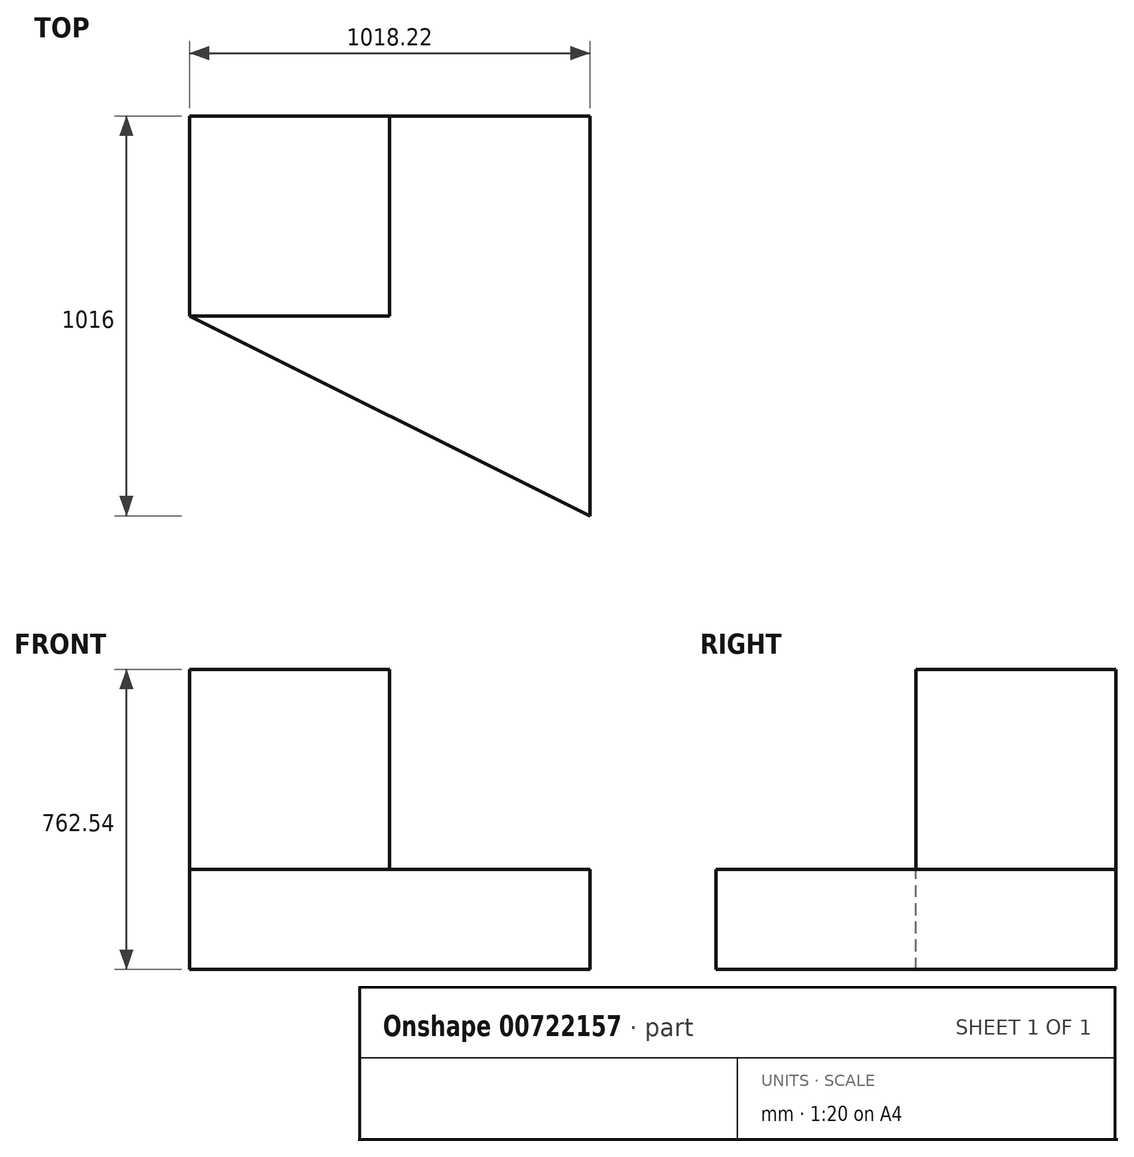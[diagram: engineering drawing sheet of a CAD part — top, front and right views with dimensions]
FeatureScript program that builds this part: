
annotation { "Feature Type Name" : "Feature", "Feature Type Description" : "" }
export const myFeature = defineFeature(function(context is Context, id is Id, definition is map)
    precondition{}
    {
        {
            var Q0;
            Q0=qCreatedBy(makeId("Front.planeOp"),FACE);
            var sketch = newSketch(context, id + "F0", { "sketchPlane" : qUnion([Q0])});
            skLineSegment(sketch, "E0", {"start": v(0, 0) * mm, "end": v(0, 762.54) * mm});
            skLineSegment(sketch, "E1", {"start": v(0, 762.54) * mm, "end": v(1018.22, 762.54) * mm});
            skLineSegment(sketch, "E2", {"start": v(1018.22, 762.54) * mm, "end": v(1018.22, 0) * mm});
            skLineSegment(sketch, "E3", {"start": v(1018.22, 0) * mm, "end": v(0, 0) * mm});
            skSolve(sketch);
        }
        {
            var Q0;
            Q0=makeQuery(id+"F0.imprint","IMPRINT",FACE,{"disambiguationData":[TD([[makeQuery(id+"F0.imprint","IMPRINT",EDGE,{"derivedFrom":sQuery(id+"F0.wireOp",EDGE,"E0")}),-1.0]])]});
            extrude(context, id + "F1", {"entities" : qUnion([Q0]), "depth" : 1016 * mm, "offsetDistance" : 25.4 * mm});
        }
        {
            var Q0;
            Q0=makeQuery(id+"F1.opExtrude","SWEPT_FACE",FACE,{"disambiguationData":[OSD([sQuery(id+"F0.wireOp",EDGE,"E1")])]});
            var sketch = newSketch(context, id + "F2", { "sketchPlane" : qUnion([Q0])});
            skLineSegment(sketch, "E4", {"start": v(0, -508) * mm, "end": v(0, -1016) * mm});
            skLineSegment(sketch, "E5", {"start": v(0, -1016) * mm, "end": v(1018.22, -1016) * mm});
            skLineSegment(sketch, "E6", {"start": v(0, -508) * mm, "end": v(1018.22, -1016) * mm});
            skSolve(sketch);
        }
        {
            var Q0;
            Q0=makeQuery(id+"F2.imprint","IMPRINT",FACE,{"disambiguationData":[TD([[makeQuery(id+"F2.imprint","IMPRINT",EDGE,{"derivedFrom":sQuery(id+"F2.wireOp",EDGE,"E4")}),-1.0]])]});
            extrude(context, id + "F3", {"entities" : qUnion([Q0]), "operationType" : NewBodyOperationType.REMOVE, "oppositeDirection" : true, "depth" : 784.86 * mm, "offsetDistance" : 25.4 * mm});
        }
        {
            var Q0;
            Q0=makeQuery(id+"F1.opExtrude","SWEPT_FACE",FACE,{"disambiguationData":[OSD([sQuery(id+"F0.wireOp",EDGE,"E1")])]});
            var sketch = newSketch(context, id + "F4", { "sketchPlane" : qUnion([Q0])});
            skLineSegment(sketch, "E7", {"start": v(0, -508) * mm, "end": v(1018.22, -508) * mm});
            skLineSegment(sketch, "E8", {"start": v(0, -508) * mm, "end": v(1018.22, -1016) * mm});
            skLineSegment(sketch, "E9", {"start": v(1018.22, -1016) * mm, "end": v(1018.22, -508) * mm});
            skSolve(sketch);
        }
        {
            var Q0;
            Q0=makeQuery(id+"F4.imprint","IMPRINT",FACE,{"disambiguationData":[TD([[makeQuery(id+"F4.imprint","IMPRINT",EDGE,{"derivedFrom":sQuery(id+"F4.wireOp",EDGE,"E7")}),-1.0]])]});
            extrude(context, id + "F5", {"entities" : qUnion([Q0]), "operationType" : NewBodyOperationType.REMOVE, "oppositeDirection" : true, "depth" : 508 * mm, "offsetDistance" : 25.4 * mm});
        }
        {
            var Q0;
            Q0=makeQuery(id+"F5.boolean.opBoolean","COPY",FACE,{"derivedFrom":makeQuery(id+"F5.opExtrude","SWEPT_FACE",FACE,{"disambiguationData":[OSD([sQuery(id+"F4.wireOp",EDGE,"E7")])]})});
            var sketch = newSketch(context, id + "F6", { "sketchPlane" : qUnion([Q0])});
            skLineSegment(sketch, "E10", {"start": v(509.11, 762.54) * mm, "end": v(509.11, 254.54) * mm});
            skLineSegment(sketch, "E11", {"start": v(509.11, 254.54) * mm, "end": v(1018.22, 254.54) * mm});
            skLineSegment(sketch, "E12", {"start": v(1018.22, 254.54) * mm, "end": v(1018.22, 762.54) * mm});
            skLineSegment(sketch, "E13", {"start": v(1018.22, 762.54) * mm, "end": v(509.11, 762.54) * mm});
            skSolve(sketch);
        }
        {
            var Q0;
            Q0=makeQuery(id+"F6.imprint","IMPRINT",FACE,{"disambiguationData":[TD([[makeQuery(id+"F6.imprint","IMPRINT",EDGE,{"derivedFrom":sQuery(id+"F6.wireOp",EDGE,"E10")}),1.0]])]});
            extrude(context, id + "F7", {"entities" : qUnion([Q0]), "operationType" : NewBodyOperationType.REMOVE, "oppositeDirection" : true, "depth" : 543.56 * mm, "offsetDistance" : 25.4 * mm});
        }
    });
